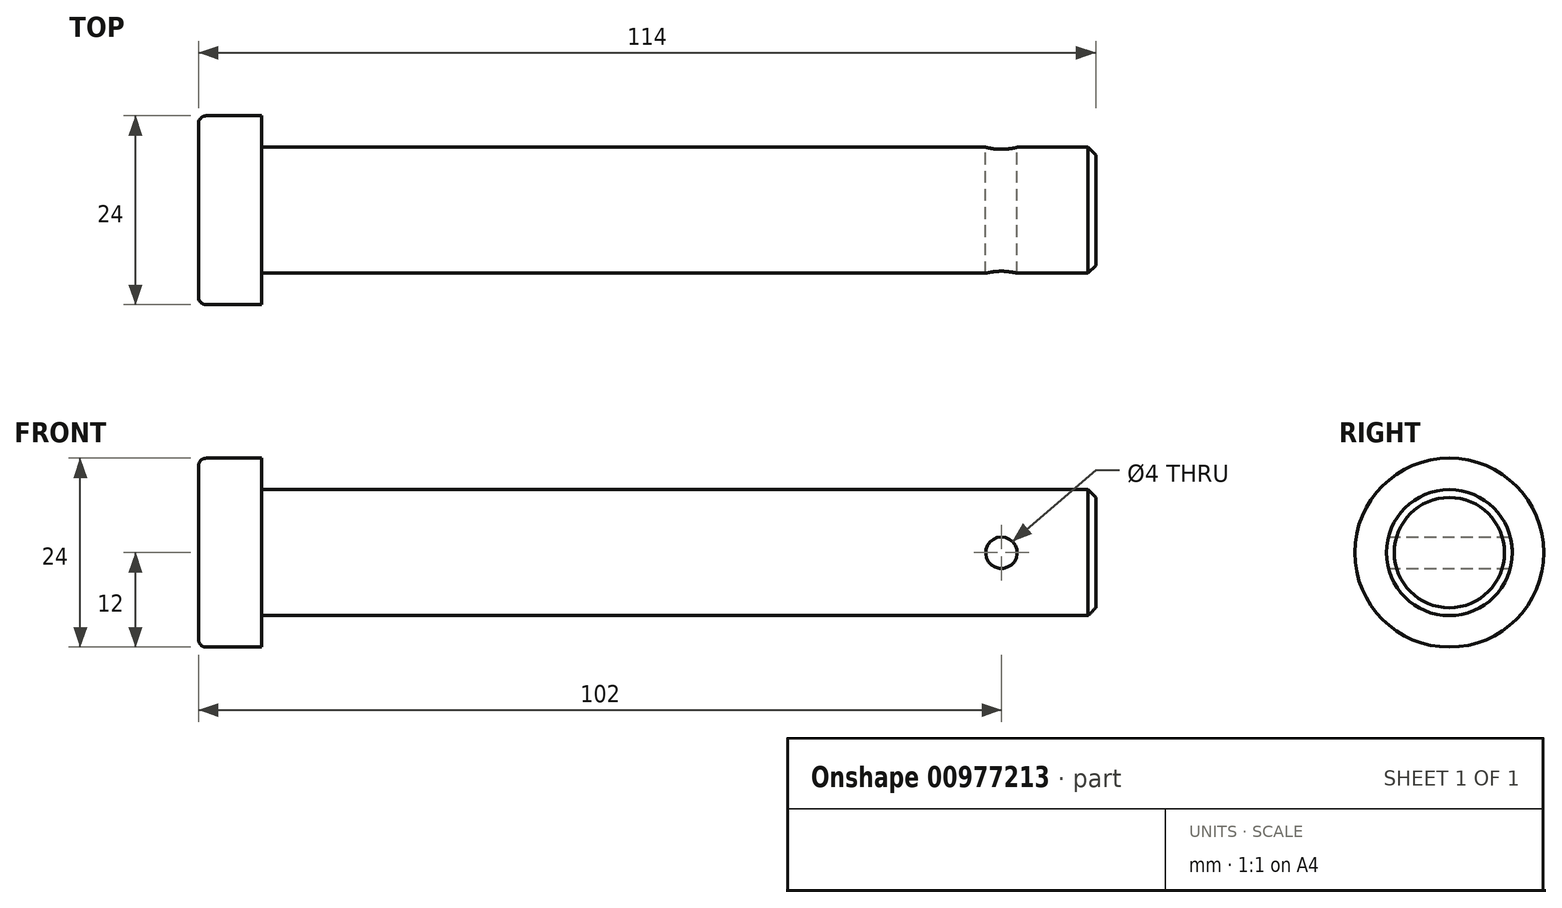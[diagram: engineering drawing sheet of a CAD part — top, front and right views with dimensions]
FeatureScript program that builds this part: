
annotation { "Feature Type Name" : "Feature", "Feature Type Description" : "" }
export const myFeature = defineFeature(function(context is Context, id is Id, definition is map)
    precondition{}
    {
        {
            var Q0;
            Q0=qCreatedBy(makeId("Right.planeOp"),FACE);
            var sketch = newSketch(context, id + "F0", { "sketchPlane" : qUnion([Q0])});
            skCircle(sketch, "E0", {"center": v(0, 0) * mm, "radius": 12 * mm});
            skSolve(sketch);
        }
        {
            var Q0;
            Q0 = qSketchRegion(id + "F0", true);
            extrude(context, id + "F1", {"entities" : qUnion([Q0]), "depth" : 8 * mm, "offsetDistance" : 25 * mm});
        }
        {
            var Q0;
            Q0=makeQuery(id+"F1.opExtrude","CAP_EDGE",EDGE,{"disambiguationData":[OSD([sQuery(id+"F0.wireOp",EDGE,"E0")])],"isStart":true});
            fillet(context, id + "F2", {"entities" : qUnion([Q0]), "radius" : 1 * mm, "tangentPropagation" : true, "allowEdgeOverflow" : false});
        }
        {
            var Q0;
            Q0=makeQuery(id+"F1.opExtrude","CAP_FACE",FACE,{"disambiguationData":[OSD([sQuery(id+"F0.wireOp",EDGE,"E0")])],"isStart":false});
            var sketch = newSketch(context, id + "F3", { "sketchPlane" : qUnion([Q0])});
            skCircle(sketch, "E1", {"center": v(0, 0) * mm, "radius": 8 * mm});
            skSolve(sketch);
        }
        {
            var Q0;
            Q0 = qSketchRegion(id + "F3", true);
            extrude(context, id + "F4", {"entities" : qUnion([Q0]), "operationType" : NewBodyOperationType.ADD, "depth" : 105 * mm, "offsetDistance" : 25 * mm});
        }
        {
            var Q0;
            Q0=makeQuery(id+"F4.opExtrude","CAP_FACE",FACE,{"disambiguationData":[OSD([sQuery(id+"F3.wireOp",EDGE,"E1")])],"isStart":false});
            var sketch = newSketch(context, id + "F5", { "sketchPlane" : qUnion([Q0])});
            skCircle(sketch, "E2.0", {"center": v(0, 0) * mm, "radius": 8 * mm});
            skSolve(sketch);
        }
        {
            var Q0;
            Q0=makeQuery(id+"F5.imprint","IMPRINT",FACE,{"disambiguationData":[TD([[makeQuery(id+"F5.imprint","IMPRINT",EDGE,{"derivedFrom":sQuery(id+"F5.wireOp",EDGE,"E2.0")}),1.0]])]});
            var sketch = newSketch(context, id + "F6", { "sketchPlane" : qUnion([Q0])});
            skCircle(sketch, "E3.0", {"center": v(0, 0) * mm, "radius": 8 * mm});
            skSolve(sketch);
        }
        {
            var Q0;
            Q0 = qSketchRegion(id + "F6", true);
            extrude(context, id + "F7", {"entities" : qUnion([Q0]), "operationType" : NewBodyOperationType.ADD, "depth" : 1 * mm, "offsetDistance" : 25 * mm});
        }
        {
            var Q0;
            Q0=makeQuery(id+"F7.opExtrude","CAP_EDGE",EDGE,{"disambiguationData":[OSD([sQuery(id+"F6.wireOp",EDGE,"E3.0")])],"isStart":false});
            chamfer(context, id + "F8", {"entities" : qUnion([Q0]), "width" : 1 * mm, "tangentPropagation" : true});
        }
        {
            var Q0;
            Q0=qCreatedBy(makeId("Front.planeOp"),FACE);
            var sketch = newSketch(context, id + "F9", { "sketchPlane" : qUnion([Q0])});
            skCircle(sketch, "E4", {"center": v(102, 0) * mm, "radius": 2 * mm});
            skSolve(sketch);
        }
        {
            var Q0;
            Q0 = qSketchRegion(id + "F9", true);
            extrude(context, id + "F10", {"entities" : qUnion([Q0]), "operationType" : NewBodyOperationType.REMOVE, "endBound" : BoundingType.SYMMETRIC, "depth" : 25 * mm, "offsetDistance" : 25 * mm});
        }
    });
